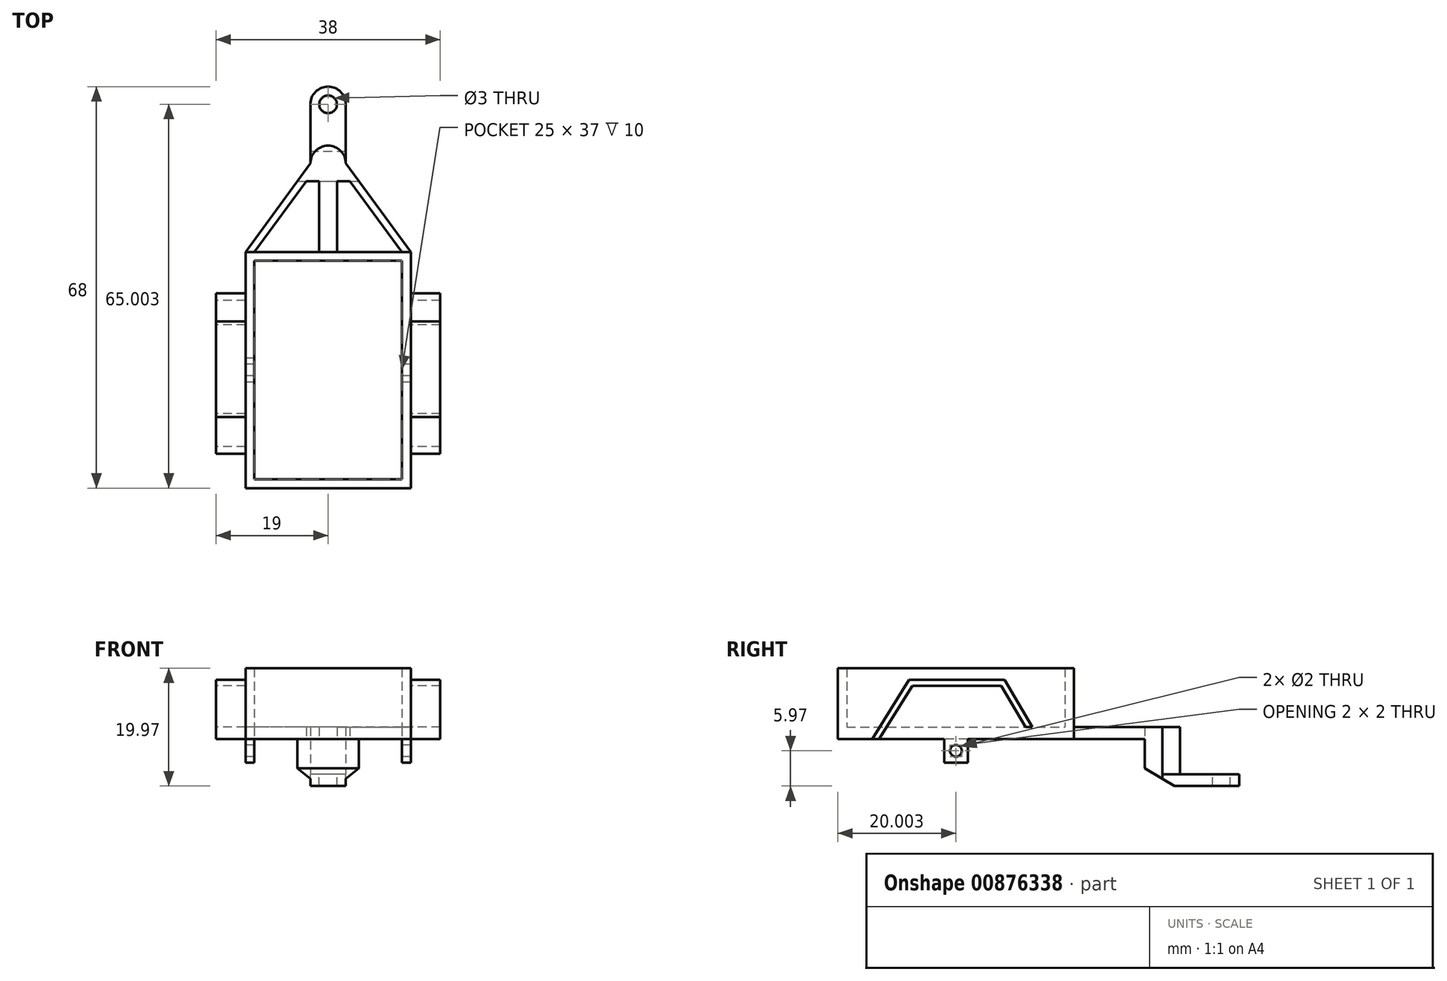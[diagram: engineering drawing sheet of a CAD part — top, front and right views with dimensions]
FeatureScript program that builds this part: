
annotation { "Feature Type Name" : "Feature", "Feature Type Description" : "" }
export const myFeature = defineFeature(function(context is Context, id is Id, definition is map)
    precondition{}
    {
        {
            var Q0;
            Q0=qCreatedBy(makeId("Top.planeOp"),FACE);
            var sketch = newSketch(context, id + "F0", { "sketchPlane" : qUnion([Q0])});
            skLineSegment(sketch, "E0.bottom", {"start": v(-14, 24.8) * mm, "end": v(14, 24.8) * mm});
            skLineSegment(sketch, "E0.top", {"start": v(-14, -15.2) * mm, "end": v(14, -15.2) * mm});
            skLineSegment(sketch, "E0.left", {"start": v(-14, 24.8) * mm, "end": v(-14, -15.2) * mm});
            skLineSegment(sketch, "E0.right", {"start": v(14, 24.8) * mm, "end": v(14, -15.2) * mm});
            skLineSegment(sketch, "E1.bottom", {"start": v(-12.5, 23.3) * mm, "end": v(12.5, 23.3) * mm});
            skLineSegment(sketch, "E1.top", {"start": v(-12.5, -13.7) * mm, "end": v(12.5, -13.7) * mm});
            skLineSegment(sketch, "E1.left", {"start": v(-12.5, 23.3) * mm, "end": v(-12.5, -13.7) * mm});
            skLineSegment(sketch, "E1.right", {"start": v(12.5, 23.3) * mm, "end": v(12.5, -13.7) * mm});
            skLineSegment(sketch, "E2", {"start": v(0, 24.8) * mm, "end": v(0, 39.8) * mm});
            skCircle(sketch, "E3", {"center": v(0, 39.8) * mm, "radius": 1.5 * mm});
            skPoint(sketch, "E4", {"position": v(0, 42.8) * mm});
            skLineSegment(sketch, "E5", {"start": v(0, 39.8) * mm, "end": v(3, 39.8) * mm});
            skLineSegment(sketch, "E6", {"start": v(3, 39.8) * mm, "end": v(-3, 39.8) * mm});
            skArc(sketch, "E7", {"start": v(3, 39.8) * mm, "mid": v(0, 42.8) * mm, "end": v(-3, 39.8) * mm});
            skLineSegment(sketch, "E8", {"start": v(-3, 39.8) * mm, "end": v(-14, 24.8) * mm});
            skLineSegment(sketch, "E9", {"start": v(3, 39.8) * mm, "end": v(14, 24.8) * mm});
            skPoint(sketch, "E10", {"position": v(0, 36.8) * mm});
            skLineSegment(sketch, "E11", {"start": v(0, 36.8) * mm, "end": v(5.2, 36.8) * mm});
            skLineSegment(sketch, "E12", {"start": v(5.2, 36.8) * mm, "end": v(-5.2, 36.8) * mm});
            skPoint(sketch, "E13", {"position": v(-3.7, 36.8) * mm});
            skPoint(sketch, "E14", {"position": v(3.7, 36.8) * mm});
            skPoint(sketch, "E15", {"position": v(-12.5, 24.8) * mm});
            skPoint(sketch, "E16", {"position": v(12.5, 24.8) * mm});
            skPoint(sketch, "E17", {"position": v(-1.5, 36.8) * mm});
            skPoint(sketch, "E18", {"position": v(1.5, 36.8) * mm});
            skLineSegment(sketch, "E19", {"start": v(-3.7, 36.8) * mm, "end": v(-12.5, 24.8) * mm});
            skLineSegment(sketch, "E20", {"start": v(3.7, 36.8) * mm, "end": v(12.5, 24.8) * mm});
            skLineSegment(sketch, "E21", {"start": v(-1.5, 36.8) * mm, "end": v(-1.5, 24.8) * mm});
            skLineSegment(sketch, "E22", {"start": v(1.5, 36.8) * mm, "end": v(1.5, 24.8) * mm});
            skLineSegment(sketch, "E23", {"start": v(-3, 39.8) * mm, "end": v(-3, 49.8) * mm});
            skLineSegment(sketch, "E24", {"start": v(3, 39.8) * mm, "end": v(3, 49.8) * mm});
            skLineSegment(sketch, "E25", {"start": v(-3, 49.8) * mm, "end": v(3, 49.8) * mm});
            skCircle(sketch, "E26", {"center": v(0, 49.8) * mm, "radius": 1.5 * mm});
            skPoint(sketch, "E27", {"position": v(0, 52.8) * mm});
            skArc(sketch, "E28", {"start": v(3, 49.8) * mm, "mid": v(0, 52.8) * mm, "end": v(-3, 49.8) * mm});
            skLineSegment(sketch, "E29", {"start": v(14, 6.8) * mm, "end": v(-14, 6.8) * mm});
            skLineSegment(sketch, "E30", {"start": v(-14, 2.8) * mm, "end": v(14, 2.8) * mm});
            skLineSegment(sketch, "E31", {"start": v(-14, 4.8) * mm, "end": v(14, 4.8) * mm});
            skSolve(sketch);
        }
        {
            var Q0;
            {var subQ3=sQuery(id+"F0.wireOp",EDGE,"E19");Q0=makeQuery(id+"F0.imprint","IMPRINT",FACE,{"disambiguationData":[TD([[makeQuery(id+"F0.imprint","IMPRINT",EDGE,{"derivedFrom":subQ3}),-1.0]])]});}
            var Q1;
            {var subQ3=sQuery(id+"F0.wireOp",EDGE,"E20");Q1=makeQuery(id+"F0.imprint","IMPRINT",FACE,{"disambiguationData":[TD([[makeQuery(id+"F0.imprint","IMPRINT",EDGE,{"derivedFrom":subQ3}),1.0]])]});}
            var Q2;
            {var subQ1=sQuery(id+"F0.wireOp",EDGE,"E0.top");Q2=makeQuery(id+"F0.imprint","IMPRINT",FACE,{"disambiguationData":[TD([[makeQuery(id+"F0.imprint","IMPRINT",EDGE,{"derivedFrom":subQ1}),1.0]])]});}
            var Q3;
            {var subQ0=sQuery(id+"F0.wireOp",EDGE,"E29");var subQ1=sQuery(id+"F0.wireOp",EDGE,"E0.left");var subQ2=makeQuery(id+"F0.imprint","INTERSECT",VERTEX,{"derivedFrom":[subQ1,subQ0]});Q3=makeQuery(id+"F0.imprint","IMPRINT",FACE,{"disambiguationData":[TD([[makeQuery(id+"F0.imprint","IMPRINT",EDGE,{"disambiguationData":[TD([[subQ2,-1.0]])],"derivedFrom":subQ1}),1.0]])]});}
            var Q4;
            {var subQ0=sQuery(id+"F0.wireOp",EDGE,"E30");var subQ1=sQuery(id+"F0.wireOp",EDGE,"E0.left");var subQ2=makeQuery(id+"F0.imprint","INTERSECT",VERTEX,{"derivedFrom":[subQ1,subQ0]});Q4=makeQuery(id+"F0.imprint","IMPRINT",FACE,{"disambiguationData":[TD([[makeQuery(id+"F0.imprint","IMPRINT",EDGE,{"disambiguationData":[TD([[subQ2,1.0]])],"derivedFrom":subQ1}),1.0]])]});}
            var Q5;
            {var subQ0=sQuery(id+"F0.wireOp",EDGE,"E29");var subQ1=sQuery(id+"F0.wireOp",EDGE,"E0.right");var subQ2=makeQuery(id+"F0.imprint","INTERSECT",VERTEX,{"derivedFrom":[subQ1,subQ0]});Q5=makeQuery(id+"F0.imprint","IMPRINT",FACE,{"disambiguationData":[TD([[makeQuery(id+"F0.imprint","IMPRINT",EDGE,{"disambiguationData":[TD([[subQ2,-1.0]])],"derivedFrom":subQ1}),-1.0]])]});}
            var Q6;
            {var subQ0=sQuery(id+"F0.wireOp",EDGE,"E30");var subQ1=sQuery(id+"F0.wireOp",EDGE,"E0.right");var subQ2=makeQuery(id+"F0.imprint","INTERSECT",VERTEX,{"derivedFrom":[subQ1,subQ0]});Q6=makeQuery(id+"F0.imprint","IMPRINT",FACE,{"disambiguationData":[TD([[makeQuery(id+"F0.imprint","IMPRINT",EDGE,{"disambiguationData":[TD([[subQ2,1.0]])],"derivedFrom":subQ1}),-1.0]])]});}
            var Q7;
            {var subQ5=sQuery(id+"F0.wireOp",EDGE,"E12");var subQ8=sQuery(id+"F0.wireOp",EDGE,"E2");var subQ10=makeQuery(id+"F0.imprint","INTERSECT",VERTEX,{"derivedFrom":[subQ8,subQ5]});Q7=makeQuery(id+"F0.imprint","IMPRINT",FACE,{"disambiguationData":[TD([[makeQuery(id+"F0.imprint","IMPRINT",EDGE,{"disambiguationData":[TD([[subQ10,-1.0]])],"derivedFrom":subQ8}),1.0]])]});}
            var Q8;
            {var subQ3=sQuery(id+"F0.wireOp",EDGE,"E12");var subQ6=sQuery(id+"F0.wireOp",EDGE,"E2");var subQ11=makeQuery(id+"F0.imprint","INTERSECT",VERTEX,{"derivedFrom":[subQ6,subQ3]});Q8=makeQuery(id+"F0.imprint","IMPRINT",FACE,{"disambiguationData":[TD([[makeQuery(id+"F0.imprint","IMPRINT",EDGE,{"disambiguationData":[TD([[subQ11,-1.0]])],"derivedFrom":subQ6}),-1.0]])]});}
            var Q9;
            {var subQ1=sQuery(id+"F0.wireOp",EDGE,"E1.bottom");Q9=makeQuery(id+"F0.imprint","IMPRINT",FACE,{"disambiguationData":[TD([[makeQuery(id+"F0.imprint","IMPRINT",EDGE,{"derivedFrom":subQ1}),1.0]])]});}
            var Q10;
            {var subQ3=sQuery(id+"F0.wireOp",EDGE,"E22");Q10=makeQuery(id+"F0.imprint","IMPRINT",FACE,{"disambiguationData":[TD([[makeQuery(id+"F0.imprint","IMPRINT",EDGE,{"derivedFrom":subQ3}),-1.0]])]});}
            var Q11;
            {var subQ3=sQuery(id+"F0.wireOp",EDGE,"E21");Q11=makeQuery(id+"F0.imprint","IMPRINT",FACE,{"disambiguationData":[TD([[makeQuery(id+"F0.imprint","IMPRINT",EDGE,{"derivedFrom":subQ3}),1.0]])]});}
            var Q12;
            {var subQ0=sQuery(id+"F0.wireOp",EDGE,"E6");var subQ1=sQuery(id+"F0.wireOp",EDGE,"E2");var subQ2=makeQuery(id+"F0.imprint","INTERSECT",VERTEX,{"derivedFrom":[subQ1,subQ0]});Q12=makeQuery(id+"F0.imprint","IMPRINT",FACE,{"disambiguationData":[TD([[makeQuery(id+"F0.imprint","IMPRINT",EDGE,{"disambiguationData":[TD([[subQ2,1.0]])],"derivedFrom":subQ1}),-1.0]])]});}
            var Q13;
            {var subQ0=sQuery(id+"F0.wireOp",EDGE,"E6");var subQ1=sQuery(id+"F0.wireOp",EDGE,"E2");var subQ2=makeQuery(id+"F0.imprint","INTERSECT",VERTEX,{"derivedFrom":[subQ1,subQ0]});Q13=makeQuery(id+"F0.imprint","IMPRINT",FACE,{"disambiguationData":[TD([[makeQuery(id+"F0.imprint","IMPRINT",EDGE,{"disambiguationData":[TD([[subQ2,1.0]])],"derivedFrom":subQ1}),1.0]])]});}
            var Q14;
            {var subQ0=sQuery(id+"F0.wireOp",EDGE,"E1.bottom");Q14=makeQuery(id+"F0.imprint","IMPRINT",FACE,{"disambiguationData":[TD([[makeQuery(id+"F0.imprint","IMPRINT",EDGE,{"derivedFrom":subQ0}),-1.0]])]});}
            var Q15;
            {var subQ0=sQuery(id+"F0.wireOp",EDGE,"E1.top");Q15=makeQuery(id+"F0.imprint","IMPRINT",FACE,{"disambiguationData":[TD([[makeQuery(id+"F0.imprint","IMPRINT",EDGE,{"derivedFrom":subQ0}),1.0]])]});}
            var Q16;
            {var subQ0=sQuery(id+"F0.wireOp",EDGE,"E31");var subQ1=sQuery(id+"F0.wireOp",EDGE,"E1.left");var subQ2=makeQuery(id+"F0.imprint","INTERSECT",VERTEX,{"derivedFrom":[subQ1,subQ0]});Q16=makeQuery(id+"F0.imprint","IMPRINT",FACE,{"disambiguationData":[TD([[makeQuery(id+"F0.imprint","IMPRINT",EDGE,{"disambiguationData":[TD([[subQ2,-1.0]])],"derivedFrom":subQ1}),1.0]])]});}
            var Q17;
            {var subQ0=sQuery(id+"F0.wireOp",EDGE,"E29");var subQ1=sQuery(id+"F0.wireOp",EDGE,"E1.left");var subQ2=makeQuery(id+"F0.imprint","INTERSECT",VERTEX,{"derivedFrom":[subQ1,subQ0]});Q17=makeQuery(id+"F0.imprint","IMPRINT",FACE,{"disambiguationData":[TD([[makeQuery(id+"F0.imprint","IMPRINT",EDGE,{"disambiguationData":[TD([[subQ2,-1.0]])],"derivedFrom":subQ1}),1.0]])]});}
            var Q18;
            {var subQ4=sQuery(id+"F0.wireOp",EDGE,"E7");Q18=makeQuery(id+"F0.imprint","IMPRINT",FACE,{"disambiguationData":[TD([[makeQuery(id+"F0.imprint","IMPRINT",EDGE,{"derivedFrom":subQ4}),1.0]])]});}
            var Q19;
            {var subQ0=sQuery(id+"F0.wireOp",EDGE,"E6");var subQ1=sQuery(id+"F0.wireOp",EDGE,"E3");var subQ2=makeQuery(id+"F0.imprint","INTERSECT",VERTEX,{"disambiguationData":[OD(0.0)],"derivedFrom":[subQ1,subQ0]});Q19=makeQuery(id+"F0.imprint","IMPRINT",FACE,{"disambiguationData":[TD([[makeQuery(id+"F0.imprint","IMPRINT",EDGE,{"disambiguationData":[TD([[subQ2,1.0]])],"derivedFrom":subQ1}),1.0]])]});}
            extrude(context, id + "F1", {"entities" : qUnion([Q0, Q1, Q2, Q3, Q4, Q5, Q6, Q7, Q8, Q9, Q10, Q11, Q12, Q13, Q14, Q15, Q16, Q17, Q18, Q19]), "depth" : 2 * mm, "offsetDistance" : 25 * mm});
        }
        {
            var Q0;
            {var subQ1=sQuery(id+"F0.wireOp",EDGE,"E0.top");Q0=makeQuery(id+"F0.imprint","IMPRINT",FACE,{"disambiguationData":[TD([[makeQuery(id+"F0.imprint","IMPRINT",EDGE,{"derivedFrom":subQ1}),1.0]])]});}
            var Q1;
            {var subQ1=sQuery(id+"F0.wireOp",EDGE,"E1.bottom");Q1=makeQuery(id+"F0.imprint","IMPRINT",FACE,{"disambiguationData":[TD([[makeQuery(id+"F0.imprint","IMPRINT",EDGE,{"derivedFrom":subQ1}),1.0]])]});}
            var Q2;
            {var subQ0=sQuery(id+"F0.wireOp",EDGE,"E29");var subQ1=sQuery(id+"F0.wireOp",EDGE,"E0.right");var subQ2=makeQuery(id+"F0.imprint","INTERSECT",VERTEX,{"derivedFrom":[subQ1,subQ0]});Q2=makeQuery(id+"F0.imprint","IMPRINT",FACE,{"disambiguationData":[TD([[makeQuery(id+"F0.imprint","IMPRINT",EDGE,{"disambiguationData":[TD([[subQ2,-1.0]])],"derivedFrom":subQ1}),-1.0]])]});}
            var Q3;
            {var subQ0=sQuery(id+"F0.wireOp",EDGE,"E30");var subQ1=sQuery(id+"F0.wireOp",EDGE,"E0.right");var subQ2=makeQuery(id+"F0.imprint","INTERSECT",VERTEX,{"derivedFrom":[subQ1,subQ0]});Q3=makeQuery(id+"F0.imprint","IMPRINT",FACE,{"disambiguationData":[TD([[makeQuery(id+"F0.imprint","IMPRINT",EDGE,{"disambiguationData":[TD([[subQ2,1.0]])],"derivedFrom":subQ1}),-1.0]])]});}
            var Q4;
            {var subQ0=sQuery(id+"F0.wireOp",EDGE,"E30");var subQ1=sQuery(id+"F0.wireOp",EDGE,"E0.left");var subQ2=makeQuery(id+"F0.imprint","INTERSECT",VERTEX,{"derivedFrom":[subQ1,subQ0]});Q4=makeQuery(id+"F0.imprint","IMPRINT",FACE,{"disambiguationData":[TD([[makeQuery(id+"F0.imprint","IMPRINT",EDGE,{"disambiguationData":[TD([[subQ2,1.0]])],"derivedFrom":subQ1}),1.0]])]});}
            var Q5;
            {var subQ0=sQuery(id+"F0.wireOp",EDGE,"E29");var subQ1=sQuery(id+"F0.wireOp",EDGE,"E0.left");var subQ2=makeQuery(id+"F0.imprint","INTERSECT",VERTEX,{"derivedFrom":[subQ1,subQ0]});Q5=makeQuery(id+"F0.imprint","IMPRINT",FACE,{"disambiguationData":[TD([[makeQuery(id+"F0.imprint","IMPRINT",EDGE,{"disambiguationData":[TD([[subQ2,-1.0]])],"derivedFrom":subQ1}),1.0]])]});}
            extrude(context, id + "F2", {"entities" : qUnion([Q0, Q1, Q2, Q3, Q4, Q5]), "operationType" : NewBodyOperationType.ADD, "depth" : 12 * mm, "offsetDistance" : 25 * mm});
        }
        {
            var Q0;
            {var subQ0=sQuery(id+"F0.wireOp",EDGE,"E29");var subQ1=sQuery(id+"F0.wireOp",EDGE,"E0.right");var subQ2=makeQuery(id+"F0.imprint","INTERSECT",VERTEX,{"derivedFrom":[subQ1,subQ0]});Q0=makeQuery(id+"F0.imprint","IMPRINT",FACE,{"disambiguationData":[TD([[makeQuery(id+"F0.imprint","IMPRINT",EDGE,{"disambiguationData":[TD([[subQ2,-1.0]])],"derivedFrom":subQ1}),-1.0]])]});}
            var Q1;
            {var subQ0=sQuery(id+"F0.wireOp",EDGE,"E30");var subQ1=sQuery(id+"F0.wireOp",EDGE,"E0.right");var subQ2=makeQuery(id+"F0.imprint","INTERSECT",VERTEX,{"derivedFrom":[subQ1,subQ0]});Q1=makeQuery(id+"F0.imprint","IMPRINT",FACE,{"disambiguationData":[TD([[makeQuery(id+"F0.imprint","IMPRINT",EDGE,{"disambiguationData":[TD([[subQ2,1.0]])],"derivedFrom":subQ1}),-1.0]])]});}
            var Q2;
            {var subQ0=sQuery(id+"F0.wireOp",EDGE,"E30");var subQ1=sQuery(id+"F0.wireOp",EDGE,"E0.left");var subQ2=makeQuery(id+"F0.imprint","INTERSECT",VERTEX,{"derivedFrom":[subQ1,subQ0]});Q2=makeQuery(id+"F0.imprint","IMPRINT",FACE,{"disambiguationData":[TD([[makeQuery(id+"F0.imprint","IMPRINT",EDGE,{"disambiguationData":[TD([[subQ2,1.0]])],"derivedFrom":subQ1}),1.0]])]});}
            var Q3;
            {var subQ0=sQuery(id+"F0.wireOp",EDGE,"E29");var subQ1=sQuery(id+"F0.wireOp",EDGE,"E0.left");var subQ2=makeQuery(id+"F0.imprint","INTERSECT",VERTEX,{"derivedFrom":[subQ1,subQ0]});Q3=makeQuery(id+"F0.imprint","IMPRINT",FACE,{"disambiguationData":[TD([[makeQuery(id+"F0.imprint","IMPRINT",EDGE,{"disambiguationData":[TD([[subQ2,-1.0]])],"derivedFrom":subQ1}),1.0]])]});}
            extrude(context, id + "F3", {"entities" : qUnion([Q0, Q1, Q2, Q3]), "operationType" : NewBodyOperationType.ADD, "oppositeDirection" : true, "depth" : 4 * mm, "offsetDistance" : 25 * mm});
        }
        {
            var Q0;
            {var subQ4=sQuery(id+"F0.wireOp",EDGE,"E7");Q0=makeQuery(id+"F0.imprint","IMPRINT",FACE,{"disambiguationData":[TD([[makeQuery(id+"F0.imprint","IMPRINT",EDGE,{"derivedFrom":subQ4}),1.0]])]});}
            var Q1;
            {var subQ0=sQuery(id+"F0.wireOp",EDGE,"E6");var subQ1=sQuery(id+"F0.wireOp",EDGE,"E3");var subQ2=makeQuery(id+"F0.imprint","INTERSECT",VERTEX,{"disambiguationData":[OD(0.0)],"derivedFrom":[subQ1,subQ0]});Q1=makeQuery(id+"F0.imprint","IMPRINT",FACE,{"disambiguationData":[TD([[makeQuery(id+"F0.imprint","IMPRINT",EDGE,{"disambiguationData":[TD([[subQ2,1.0]])],"derivedFrom":subQ1}),1.0]])]});}
            var Q2;
            {var subQ3=sQuery(id+"F0.wireOp",EDGE,"E12");var subQ6=sQuery(id+"F0.wireOp",EDGE,"E2");var subQ11=makeQuery(id+"F0.imprint","INTERSECT",VERTEX,{"derivedFrom":[subQ6,subQ3]});Q2=makeQuery(id+"F0.imprint","IMPRINT",FACE,{"disambiguationData":[TD([[makeQuery(id+"F0.imprint","IMPRINT",EDGE,{"disambiguationData":[TD([[subQ11,-1.0]])],"derivedFrom":subQ6}),-1.0]])]});}
            var Q3;
            {var subQ5=sQuery(id+"F0.wireOp",EDGE,"E12");var subQ8=sQuery(id+"F0.wireOp",EDGE,"E2");var subQ10=makeQuery(id+"F0.imprint","INTERSECT",VERTEX,{"derivedFrom":[subQ8,subQ5]});Q3=makeQuery(id+"F0.imprint","IMPRINT",FACE,{"disambiguationData":[TD([[makeQuery(id+"F0.imprint","IMPRINT",EDGE,{"disambiguationData":[TD([[subQ10,-1.0]])],"derivedFrom":subQ8}),1.0]])]});}
            var Q4;
            Q4=makeQuery(id+"F0.imprint","IMPRINT",FACE,{"disambiguationData":[TD([[makeQuery(id+"F0.imprint","IMPRINT",EDGE,{"derivedFrom":sQuery(id+"F0.wireOp",EDGE,"E7")}),-1.0]])]});
            var Q5;
            {var subQ0=sQuery(id+"F0.wireOp",EDGE,"E28");Q5=makeQuery(id+"F0.imprint","IMPRINT",FACE,{"disambiguationData":[TD([[makeQuery(id+"F0.imprint","IMPRINT",EDGE,{"derivedFrom":subQ0}),1.0]])]});}
            var Q6;
            {var subQ0=sQuery(id+"F0.wireOp",EDGE,"E6");var subQ1=sQuery(id+"F0.wireOp",EDGE,"E2");var subQ2=makeQuery(id+"F0.imprint","INTERSECT",VERTEX,{"derivedFrom":[subQ1,subQ0]});Q6=makeQuery(id+"F0.imprint","IMPRINT",FACE,{"disambiguationData":[TD([[makeQuery(id+"F0.imprint","IMPRINT",EDGE,{"disambiguationData":[TD([[subQ2,1.0]])],"derivedFrom":subQ1}),1.0]])]});}
            var Q7;
            {var subQ0=sQuery(id+"F0.wireOp",EDGE,"E6");var subQ1=sQuery(id+"F0.wireOp",EDGE,"E2");var subQ2=makeQuery(id+"F0.imprint","INTERSECT",VERTEX,{"derivedFrom":[subQ1,subQ0]});Q7=makeQuery(id+"F0.imprint","IMPRINT",FACE,{"disambiguationData":[TD([[makeQuery(id+"F0.imprint","IMPRINT",EDGE,{"disambiguationData":[TD([[subQ2,1.0]])],"derivedFrom":subQ1}),-1.0]])]});}
            extrude(context, id + "F4", {"entities" : qUnion([Q0, Q1, Q2, Q3, Q4, Q5, Q6, Q7]), "operationType" : NewBodyOperationType.ADD, "oppositeDirection" : true, "depth" : 7.97 * mm, "offsetDistance" : 25 * mm});
        }
        {
            var Q0;
            Q0=makeQuery(id+"F0.imprint","IMPRINT",FACE,{"disambiguationData":[TD([[makeQuery(id+"F0.imprint","IMPRINT",EDGE,{"derivedFrom":sQuery(id+"F0.wireOp",EDGE,"E7")}),-1.0]])]});
            var Q1;
            {var subQ0=sQuery(id+"F0.wireOp",EDGE,"E28");Q1=makeQuery(id+"F0.imprint","IMPRINT",FACE,{"disambiguationData":[TD([[makeQuery(id+"F0.imprint","IMPRINT",EDGE,{"derivedFrom":subQ0}),1.0]])]});}
            extrude(context, id + "F5", {"entities" : qUnion([Q0, Q1]), "operationType" : NewBodyOperationType.REMOVE, "oppositeDirection" : true, "depth" : 6 * mm, "offsetDistance" : 25 * mm});
        }
        {
            var Q0;
            Q0=makeQuery(id+"F4.opExtrude","CAP_EDGE",EDGE,{"disambiguationData":[OSD([sQuery(id+"F0.wireOp",EDGE,"E12")])],"isStart":false});
            chamfer(context, id + "F6", {"entities" : qUnion([Q0]), "chamferType" : ChamferType.TWO_OFFSETS, "width1" : 3 * mm, "oppositeDirection" : false, "width2" : 5 * mm, "tangentPropagation" : true});
        }
        {
            var Q0;
            Q0=qCreatedBy(makeId("Right.planeOp"),FACE);
            var sketch = newSketch(context, id + "F7", { "sketchPlane" : qUnion([Q0])});
            skCircle(sketch, "E32", {"center": v(4.8, -2) * mm, "radius": 1 * mm});
            skCircle(sketch, "E33", {"center": v(4.8, -2) * mm, "radius": 9.5 * mm});
            skLineSegment(sketch, "E34", {"start": v(-8.2, 0) * mm, "end": v(-2.6, 9) * mm});
            skLineSegment(sketch, "E35", {"start": v(-2.6, 9) * mm, "end": v(12.46, 9) * mm});
            skLineSegment(sketch, "E36", {"start": v(12.46, 9) * mm, "end": v(17.8, 0) * mm});
            skLineSegment(sketch, "E37", {"start": v(-9.37, 0) * mm, "end": v(-3.15, 10) * mm});
            skLineSegment(sketch, "E38", {"start": v(-3.15, 10) * mm, "end": v(13.03, 10) * mm});
            skLineSegment(sketch, "E39", {"start": v(13.03, 10) * mm, "end": v(18.97, 0) * mm});
            skLineSegment(sketch, "E40", {"start": v(-9.37, 0) * mm, "end": v(-8.2, 0) * mm});
            skLineSegment(sketch, "E41", {"start": v(17.8, 0) * mm, "end": v(18.97, 0) * mm});
            skLineSegment(sketch, "E42", {"start": v(-8.13, 2) * mm, "end": v(-6.95, 2) * mm});
            skLineSegment(sketch, "E43", {"start": v(16.62, 2) * mm, "end": v(17.78, 2) * mm});
            skSolve(sketch);
        }
        {
            var Q0;
            Q0=makeQuery(id+"F7.imprint","IMPRINT",FACE,{"disambiguationData":[TD([[makeQuery(id+"F7.imprint","IMPRINT",EDGE,{"derivedFrom":sQuery(id+"F7.wireOp",EDGE,"E32")}),1.0]])]});
            extrude(context, id + "F8", {"entities" : qUnion([Q0]), "operationType" : NewBodyOperationType.REMOVE, "endBound" : BoundingType.SYMMETRIC, "depth" : 30 * mm, "offsetDistance" : 25 * mm});
        }
        {
            var Q0;
            Q0=makeQuery(id+"F7.imprint","IMPRINT",FACE,{"disambiguationData":[TD([[makeQuery(id+"F7.imprint","IMPRINT",EDGE,{"derivedFrom":sQuery(id+"F7.wireOp",EDGE,"E34")}),1.0]])]});
            var Q1;
            {var subQ1=sQuery(id+"F7.wireOp",EDGE,"E35");Q1=makeQuery(id+"F7.imprint","IMPRINT",FACE,{"disambiguationData":[TD([[makeQuery(id+"F7.imprint","IMPRINT",EDGE,{"derivedFrom":subQ1}),1.0]])]});}
            extrude(context, id + "F9", {"entities" : qUnion([Q0, Q1]), "operationType" : NewBodyOperationType.ADD, "endBound" : BoundingType.SYMMETRIC, "depth" : 38 * mm, "offsetDistance" : 25 * mm});
        }
        {
            var Q0;
            {var subQ1=sQuery(id+"F7.wireOp",EDGE,"E35");Q0=makeQuery(id+"F7.imprint","IMPRINT",FACE,{"disambiguationData":[TD([[makeQuery(id+"F7.imprint","IMPRINT",EDGE,{"derivedFrom":subQ1}),1.0]])]});}
            extrude(context, id + "F10", {"entities" : qUnion([Q0]), "operationType" : NewBodyOperationType.REMOVE, "endBound" : BoundingType.SYMMETRIC, "depth" : 25 * mm, "offsetDistance" : 25 * mm});
        }
    });
